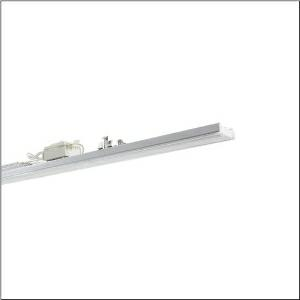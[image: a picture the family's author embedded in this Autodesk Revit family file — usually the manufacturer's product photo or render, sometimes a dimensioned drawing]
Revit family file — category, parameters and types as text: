
# Revit family: licross_21_recessed_mo_52tl12dn6axg
name_source: partatom
category: Lighting Fixtures
units: mm (PartAtom-declared; Revit-internal decimal feet)

## family parameters
Cut with Voids When Loaded = No
Host = Face
Light Source = No
Part Type = Normal
Room Calculation Point = No
Round Connector Dimension = Use Diameter
Shared = No

## types (1)
- --- (1 x LED, 10000 lm, 58 W, 6500K)
    Apparent Load = 58 VA
    CIE Flux Codes = 72 92 99 100 100
    Color Rendering = 80
    Color Temperature = 6500K
    Default Elevation = 1800 mm
    Description = Licross 21 Recessed MO, luminaire insert, of sheet steel, galvanised, coil coated, white, length: 1.500mm, width: 66mm, height: 67mm, LED rated luminous flux: 10.000lm, light colour: 865, SDCM (Standard Deviation of Colour Matching)MacAdam ≤ 3 SDCM (initial), control gear: DALI 2, with plug, 5-pole, with phase selection, mains connection: 220..240V, AC, 50/60Hz, rated input power: 58W, internal wiring halogen-free, primary optical cover: cover, of PMMA, light emission: direct distribution, primary light characteristic: symmetric, protection rating (complete): IP40, insulation class (complete): insulation class I (protective earthing), certification: CE, ENEC, VDE, UKCA, protection symbol: D if used in an environment without relevant dust loads with corresponding accessories, impact resistance: IK06, permissible ambient temperature for indoor applications: -25..+35°C, corresponds to IFS (International Featured Standards) requirements for safety and quality in the food industry, reducing of maximum allowable ambient temperature of 5°C with ceiling mounting, LABS conformity tested according to VDMA 24364:2018-05, The light source and the operating device comply with the requirements of the Ecodesign Regulation (EU) 2019/2020 and are replaceable in accordance with this regulation, packaging unit: 1 piece
    Height = 58 mm
    Lamp = 1 x LED
    Lamp Light Flux = 10000 lm
    Lamp Power = 58 W
    Lamp count = 1
    Length = 1500 mm
    Luminous efficacy = 172 lm/W
    Manufacturer = Siteco
    ModVariant = No
    Model = 52TL12DN6AXG
    Mounting Place = Ceiling
    Mounting Type = Pendant
    Number of Poles = 1
    OnlyDefault = Yes
    Power Factor = 1
    Product Name = Licross 21 Recessed MO
    Product group = luminaire insert | ceiling pendant
    ProductGroupID = 901
    Protection Class = Protection class I
    Protection Degree = IP 40
    RLX_Detail_Level = 1
    RLX_Emergency_Light_Flux = 0 lm
    RLX_Emergency_Type = 0
    RLX_Emergency_Type_DB = No
    RlxData = <blob elided: 24865 chars, md5=110d25ed>
    Socket = socket
    Standby Power = 0 W
    System Light Flux = 10000 lm
    System Power = 58 W
    Type Comments = factory setting: luminous flux: 100 % | dim-lin: 254 | 390 mA
    Type Image = l_1296930.jpg
    URL = http://relux.com
    VarID = @adj_093419
    Voltage = 0 V
    Weight = 0.00 kg
    Width = 66 mm

## geometry (parser evidence)
native form markers: Blend x4, Sweep x10
no freeform markers — native parametric forms only
